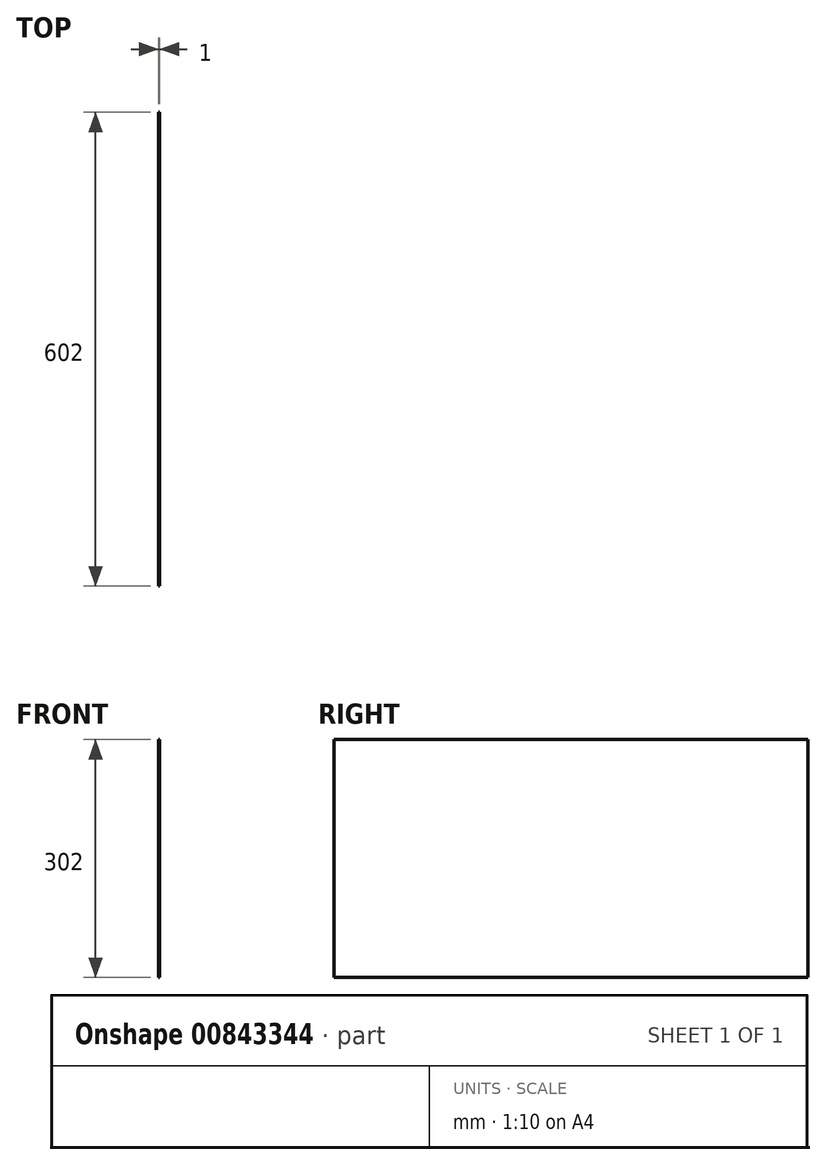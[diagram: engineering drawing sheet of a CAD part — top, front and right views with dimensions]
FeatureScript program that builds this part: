
annotation { "Feature Type Name" : "Feature", "Feature Type Description" : "" }
export const myFeature = defineFeature(function(context is Context, id is Id, definition is map)
    precondition{}
    {
        {
            var Q0;
            Q0=qCreatedBy(makeId("Right.planeOp"),FACE);
            var sketch = newSketch(context, id + "F0", { "sketchPlane" : qUnion([Q0])});
            skLineSegment(sketch, "E0.bottom", {"start": v(301, 151) * mm, "end": v(-301, 151) * mm});
            skLineSegment(sketch, "E0.top", {"start": v(301, -151) * mm, "end": v(-301, -151) * mm});
            skLineSegment(sketch, "E0.left", {"start": v(301, 151) * mm, "end": v(301, -151) * mm});
            skLineSegment(sketch, "E0.right", {"start": v(-301, 151) * mm, "end": v(-301, -151) * mm});
            skPoint(sketch, "E0.middle", {"position": v(0, 0) * mm});
            skSolve(sketch);
        }
        {
            var Q0;
            Q0=qSketchRegion(id+"F0",true);
            extrude(context, id + "F1", {"entities" : qUnion([Q0]), "depth" : 1 * mm, "offsetDistance" : 25 * mm});
        }
    });
